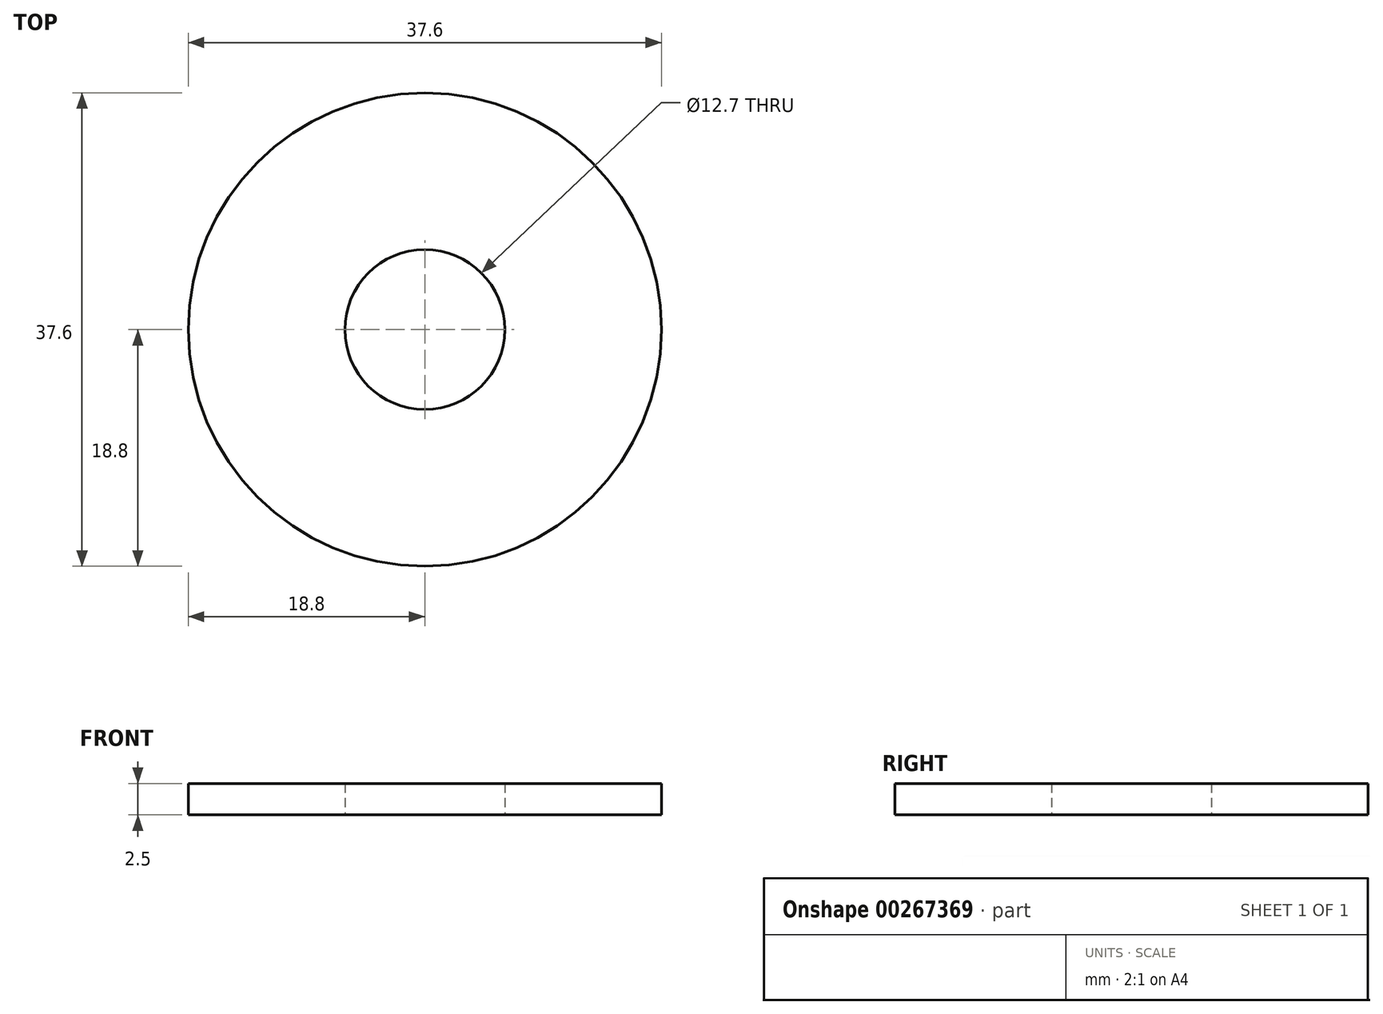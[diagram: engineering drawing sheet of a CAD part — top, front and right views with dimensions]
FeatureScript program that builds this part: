
annotation { "Feature Type Name" : "Feature", "Feature Type Description" : "" }
export const myFeature = defineFeature(function(context is Context, id is Id, definition is map)
    precondition{}
    {
        {
            var Q0;
            Q0=qCreatedBy(makeId("Top.planeOp"),FACE);
            var sketch = newSketch(context, id + "F0", { "sketchPlane" : qUnion([Q0])});
            skCircle(sketch, "E0", {"center": v(0, 0) * mm, "radius": 18.8 * mm});
            skCircle(sketch, "E1", {"center": v(0, 0) * mm, "radius": 6.35 * mm});
            skSolve(sketch);
        }
        {
            var Q0;
            Q0=makeQuery(id+"F0.imprint","IMPRINT",FACE,{"disambiguationData":[TD([[makeQuery(id+"F0.imprint","IMPRINT",EDGE,{"derivedFrom":sQuery(id+"F0.wireOp",EDGE,"E0")}),1.0]])]});
            extrude(context, id + "F1", {"entities" : qUnion([Q0]), "depth" : 2.5 * mm});
        }
    });
